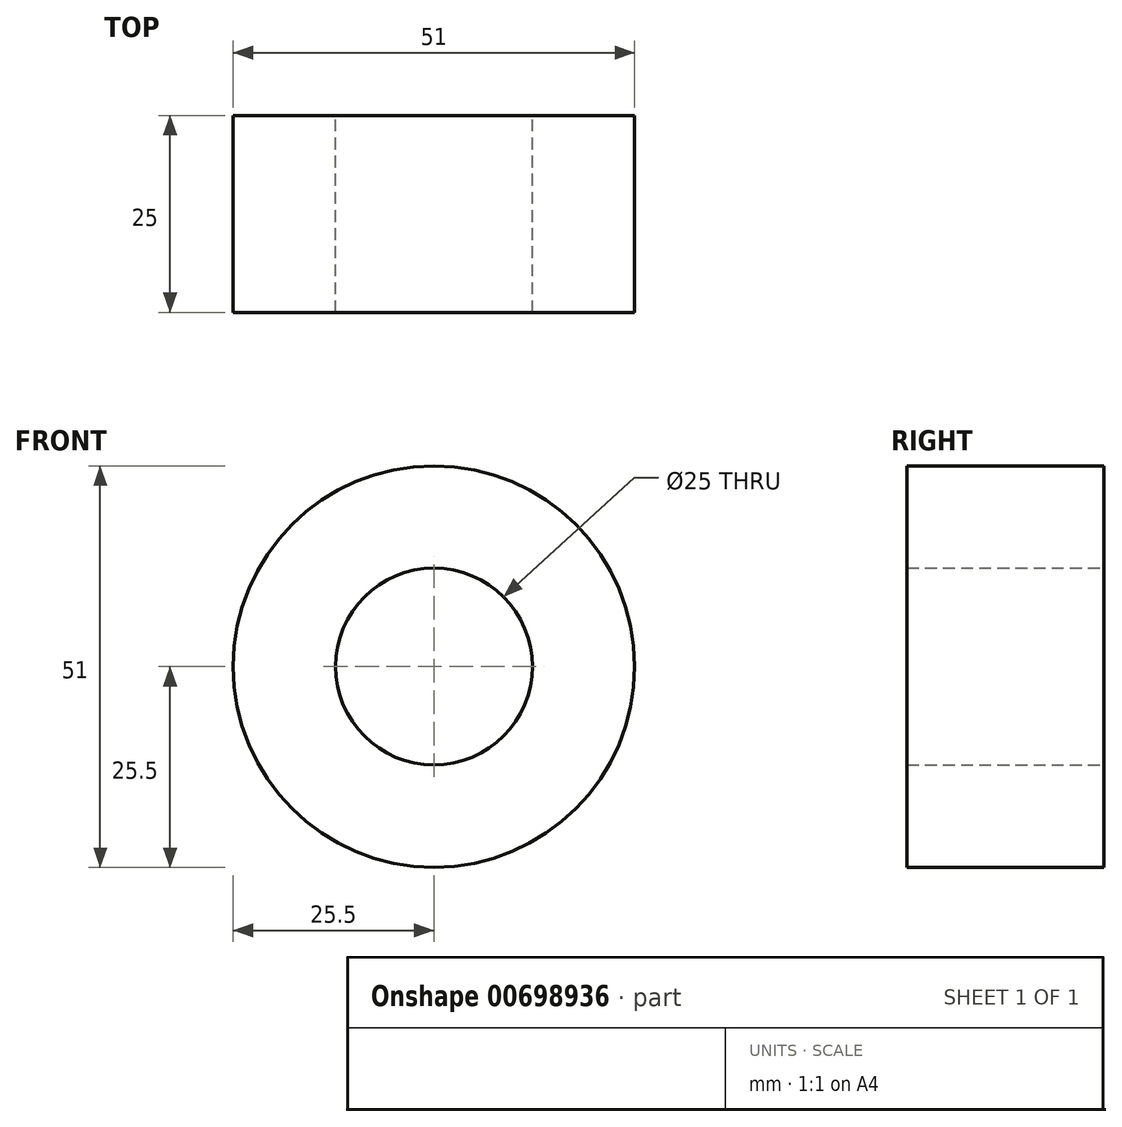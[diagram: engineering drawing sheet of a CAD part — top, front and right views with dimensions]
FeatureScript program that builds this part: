
annotation { "Feature Type Name" : "Feature", "Feature Type Description" : "" }
export const myFeature = defineFeature(function(context is Context, id is Id, definition is map)
    precondition{}
    {
        {
            var Q0;
            Q0=qCreatedBy(makeId("Front.planeOp"),FACE);
            var sketch = newSketch(context, id + "F0", { "sketchPlane" : qUnion([Q0])});
            skLineSegment(sketch, "E0.bottom", {"start": v(72.95, -73.73) * mm, "end": v(-72.95, -73.73) * mm});
            skLineSegment(sketch, "E0.top", {"start": v(72.95, 73.73) * mm, "end": v(-72.95, 73.73) * mm});
            skLineSegment(sketch, "E0.left", {"start": v(72.95, -73.73) * mm, "end": v(72.95, 73.73) * mm});
            skLineSegment(sketch, "E0.right", {"start": v(-72.95, -73.73) * mm, "end": v(-72.95, 73.73) * mm});
            skPoint(sketch, "E0.middle", {"position": v(0, 0) * mm});
            skSolve(sketch);
        }
        {
            var Q0;
            Q0=makeQuery(id+"F0.imprint","IMPRINT",FACE,{"disambiguationData":[TD([[makeQuery(id+"F0.imprint","IMPRINT",EDGE,{"derivedFrom":sQuery(id+"F0.wireOp",EDGE,"E0.bottom")}),-1.0]])]});
            var sketch = newSketch(context, id + "F1", { "sketchPlane" : qUnion([Q0])});
            skCircle(sketch, "E1", {"center": v(0, 0) * mm, "radius": 25.5 * mm});
            skCircle(sketch, "E2", {"center": v(0, 0) * mm, "radius": 12.5 * mm});
            skSolve(sketch);
        }
        {
            var Q0;
            Q0 = qSketchRegion(id + "F1", true);
            extrude(context, id + "F2", {"entities" : qUnion([Q0]), "depth" : 25 * mm, "offsetDistance" : 25 * mm});
        }
    });
